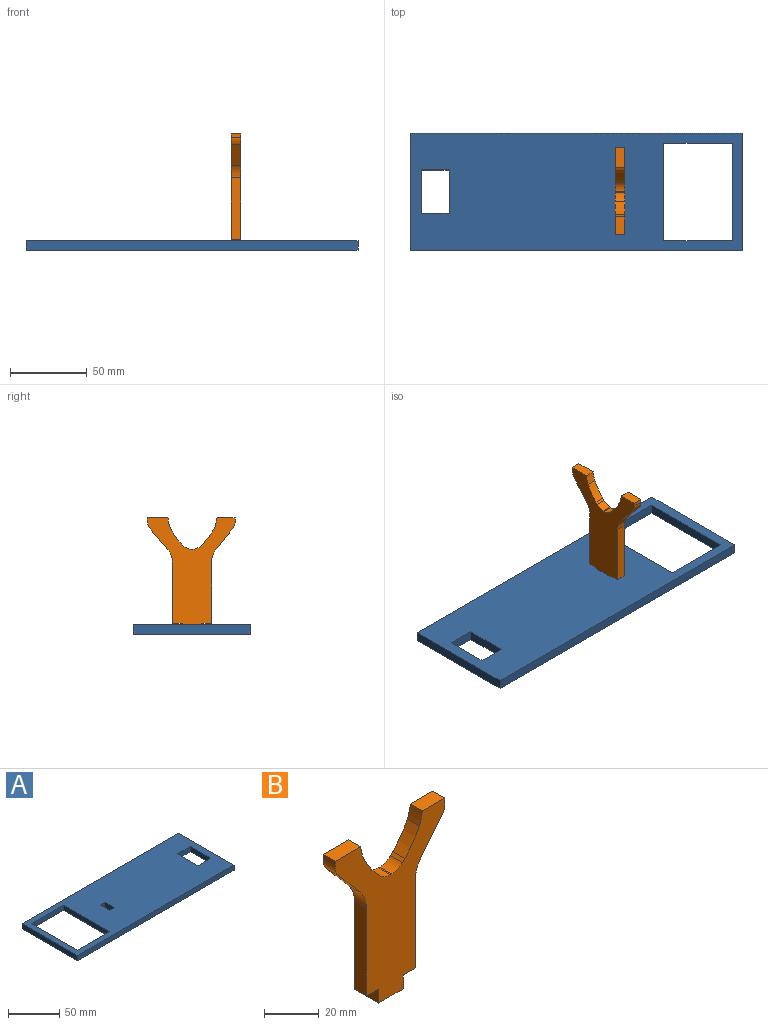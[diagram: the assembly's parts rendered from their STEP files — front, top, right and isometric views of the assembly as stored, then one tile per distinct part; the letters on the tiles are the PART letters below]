
ASSEMBLY  parts=2 mates=1
PART A: 18 faces, bbox 215.9x76.2x6.2 mm
  f0: plane 215.9x6.22mm, normal (0,1,0), area 1343.5mm2, adj f1,f15,f16,f17
  f1: plane 76.2x6.22mm, normal (-1,0,0), area 474.2mm2, adj f0,f2,f16,f17
  f2: plane 215.9x6.22mm, normal (0,-1,0), area 1343.5mm2, adj f1,f15,f16,f17
  f3: plane 28.22x6.22mm, normal (1,0,0), area 175.6mm2, adj f4,f12,f16,f17
  f4: plane 17.78x6.22mm, normal (0,-1,0), area 110.6mm2, adj f3,f5,f16,f17
  f5: plane 28.22x6.22mm, normal (-1,0,0), area 175.6mm2, adj f4,f12,f16,f17
  f6: plane 12.7x6.22mm, normal (1,0,0), area 79mm2, adj f7,f13,f16,f17
  f7: plane 6.35x6.22mm, normal (0,-1,0), area 39.5mm2, adj f6,f8,f16,f17
  f8: plane 12.7x6.22mm, normal (-1,0,0), area 79mm2, adj f7,f13,f16,f17
  f9: plane 63.5x6.22mm, normal (1,0,0), area 395.2mm2, adj f10,f14,f16,f17
  f10: plane 44.45x6.22mm, normal (0,-1,0), area 276.6mm2, adj f9,f11,f16,f17
  f11: plane 63.5x6.22mm, normal (-1,0,0), area 395.2mm2, adj f10,f14,f16,f17
  f12: plane 17.78x6.22mm, normal (0,1,0), area 110.6mm2, adj f3,f5,f16,f17
  f13: plane 6.35x6.22mm, normal (0,1,0), area 39.5mm2, adj f6,f8,f16,f17
  f14: plane 44.45x6.22mm, normal (0,1,0), area 276.6mm2, adj f9,f11,f16,f17
  f15: plane 76.2x6.22mm, normal (1,0,0), area 474.2mm2, adj f0,f2,f16,f17
  f16: plane 215.9x76.2mm, normal (0,0,1), area 13046.6mm2, adj f0,f1,f2,f3,f4,f5,f6,f7
  f17: plane 215.9x76.2mm, normal (0,0,-1), area 13046.6mm2, adj f0,f1,f2,f3,f4,f5,f6,f7
PART B: 28 faces, bbox 57x6.2x74.8 mm
  f0: plane 6.22x1.27mm, normal (0.73,0,0.69), area 10.9mm2, adj f18,f19,f20,f27
  f1: plane 13.2x6.22mm, normal (0,0,1), area 82.2mm2, adj f2,f18,f19,f26
  f2: plane 6.22x2.23mm, normal (-1,0,0), area 13.9mm2, adj f1,f18,f19,f21
  f3: plane 13.32x11.36mm, normal (-0.76,0,-0.65), area 108.9mm2, adj f4,f18,f19,f21
  f4: cylinder r=12.7mm len=8.24mm, axis (0,1,0), area 55.8mm2, adj f3,f5,f18,f19
  f5: plane 39.77x6.22mm, normal (-1,0,0), area 247.5mm2, adj f4,f6,f18,f19
  f6: plane 6.35x6.22mm, normal (0,0,-1), area 39.5mm2, adj f5,f7,f18,f19
  f7: plane 6.25x6.22mm, normal (-1,0,0), area 38.9mm2, adj f6,f8,f18,f19
  f8: plane 12.7x6.22mm, normal (0,0,-1), area 79mm2, adj f7,f9,f18,f19
  f9: plane 6.25x6.22mm, normal (1,0,0), area 38.9mm2, adj f8,f10,f18,f19
  f10: plane 6.35x6.22mm, normal (0,0,-1), area 39.5mm2, adj f9,f11,f18,f19
  f11: plane 39.97x6.22mm, normal (1,0,0), area 248.8mm2, adj f10,f12,f18,f19
  f12: cylinder r=12.7mm len=7.96mm, axis (0,1,0), area 53.6mm2, adj f11,f13,f18,f19
  f13: plane 13.44x10.82mm, normal (0.78,0,-0.63), area 107.4mm2, adj f12,f18,f19,f22
  f14: plane 6.22x2.36mm, normal (1,0,0), area 14.7mm2, adj f15,f18,f19,f22
  f15: plane 11.7x6.22mm, normal (0,0,1), area 72.8mm2, adj f14,f18,f19,f25
  f16: plane 6.22x1.3mm, normal (-0.71,0,0.7), area 11.4mm2, adj f18,f19,f23,f24
  f17: plane 6.22x0.76mm, normal (0,0,1), area 4.7mm2, adj f18,f19,f20,f23
  f18: plane 74.83x56.97mm, normal (0,-1,0), area 1822.6mm2, adj f0,f1,f2,f3,f4,f5,f6,f7
  f19: plane 74.83x56.97mm, normal (0,1,0), area 1822.6mm2, adj f0,f1,f2,f3,f4,f5,f6,f7
  f20: cylinder r=7.73mm len=6.22mm, axis (0,1,0), area 39.1mm2, adj f0,f17,f18,f19
  f21: cylinder r=7.73mm len=6.22mm, axis (0,-1,0), area 34mm2, adj f2,f3,f18,f19
  f22: cylinder r=7.73mm len=6.22mm, axis (0,-1,0), area 32.6mm2, adj f13,f14,f18,f19
  f23: cylinder r=7.73mm len=6.22mm, axis (0,-1,0), area 38.2mm2, adj f16,f17,f18,f19
  f24: cylinder r=39.77mm len=10.68mm, axis (0,-1,0), area 81.6mm2, adj f16,f18,f19,f25
  f25: cylinder r=39.77mm len=6.22mm, axis (0,1,0), area 38.9mm2, adj f15,f18,f19,f24
  f26: cylinder r=39.77mm len=6.22mm, axis (0,-1,0), area 39.6mm2, adj f1,f18,f19,f27
  f27: cylinder r=39.77mm len=10.47mm, axis (0,-1,0), area 79.2mm2, adj f0,f18,f19,f26
PLACE A rot(axis=(0,1,0),180deg) t=(-80.08,89.87,8.62)mm
PLACE B rot(axis=(0,0,-1),90deg) t=(-56.21,50.71,3.22)mm
MATE parallel A.f8 <-> B.f18  axis (1,0,0) through (-62.43,50.71,5.5)mm
